# Revit family: QF_FESTIVE_YC18
name_source: partatom
category: Specialty Equipment
units: mm (PartAtom-declared; Revit-internal decimal feet)

## family parameters
Always vertical = Yes
Cut with Voids When Loaded = No
Part Type = Normal
Room Calculation Point = No
Round Connector Dimension = Use Diameter
Shared = No
Work Plane-Based = No

## types (1)
- YC18_220-240/50/1
    Apparent Power = 1276 VA
    Conn Conduit = Yes
    Conn Plug = 10A Plug
    Control Panel A = No
    Control Panel B = Yes
    Cycle = 50 Hz
    Default Elevation = 0 mm  [stored 0 ft]
    Depth = 640 mm  [stored 2.09974 ft]
    Description = YORK CHILLED
    Elec Conn Connection Height = 0 mm  [stored 0 ft]
    Elec Conn RI Height = 0 mm  [stored 0 ft]
    FL Amps = 6 A
    Foodservice Equipment Identifier = Yes
    Height = 1400 mm  [stored 4.59318 ft]
    Identify Quantity as Lot = Yes
    Length = 1770 mm
    Manufacturer = FESTIVE
    Max Overcurrent Protection = 0 A
    Min Ckt Ampacity = 0 A
    Model = YC18
    Number of Poles = 1
    Offset = 275 mm  [stored 0.902231 ft]
    Pan 2 = Yes
    Pan 3 = Yes
    Pan Length = 580 mm  [stored 1.90289 ft]
    Panel Length = 576 mm  [stored 1.88976 ft]
    Panel Offset = 250 mm  [stored 0.82021 ft]
    Phase = 1
    Shelf 2 = Yes
    Volts = 220 V
    Watts = 1276 W
    Weight in Pounds = 0

note: [stored X ft] marks values corroborated as IEEE doubles in the binary element streams (Revit-internal decimal feet)

## geometry (parser evidence)
native form markers: Sweep x6
no freeform markers — native parametric forms only
